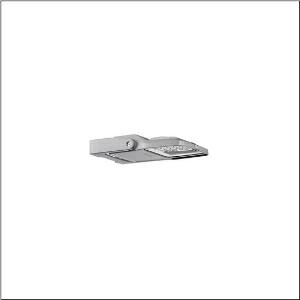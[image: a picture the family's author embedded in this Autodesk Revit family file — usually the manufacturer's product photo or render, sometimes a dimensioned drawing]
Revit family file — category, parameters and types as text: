
# Revit family: floodlight_fl_21_iq_micro___pl33t_5xa7761a2f2a_98c0
name_source: partatom
category: Lighting Fixtures
units: mm (PartAtom-declared; Revit-internal decimal feet)

## family parameters
Cut with Voids When Loaded = No
Host = Face
Light Source = No
Part Type = Normal
Room Calculation Point = No
Round Connector Dimension = Use Diameter
Shared = No

## types (1)
- --- (1 x LED, 2930 lm, 23.1 W, 3000K)
    Apparent Load = 23 VA
    CIE Flux Codes = 26 75 99 100 100
    Color Rendering = 70
    Color Temperature = 3000K
    Default Elevation = 1800 mm
    Description = Floodlight FL 21 iQ micro, floodlight, primary light control with lens, of PMMA, primary optical cover: protective disc, of toughened safety glass, transparent, light distribution: PL33T, light emission: direct distribution, installation type: surface-mounted, LED, High Power LED, rated luminous flux: 2.930lm, luminous efficacy: 127lm/W, light colour: 730, colour temperature: 3000K, control: optimised constant luminous flux control (CLO 2.0), Desk-Remote (wireless, voltage-free reading and setting of iQ features in the workshop via application-optimized NFC function/RFID function), Light-Fading, Smart-Wire, Night-Set, Lumen-Switch, Temp-Guard, Auto-Match, with terminal, 6-pole, mains connection: 220..240V, AC, 50/60Hz, start of lifetime: 23W, end of service life: 24W, reduction: 11W, luminaire housing, of diecast aluminium, powder-coated, Siteco® metallic grey (DB 702S), corrosivity category C5 mid according to DIN EN ISO 12944, sealing non-destructively replaceable, design bracket, of diecast aluminium, powder-coated, Siteco® metallic grey (DB 702S), protection rating (complete): IP66, insulation class (complete): insulation class II (safety insulation), certification: CE, ENEC, VDE, protection symbol: D, impact resistance: IK07, permissible operating ambient temperature: -40..+40°C, permissible operating ambient temperature for outdoor applications: -40..+50°C, standard: DIN EN 12944, LABS conformity tested according to VDMA 24364:2018-05, packaging unit: 1 piece

Light Distribution: PL33T
    Height = 65 mm
    Lamp = 1 x LED
    Lamp Light Flux = 2930 lm
    Lamp Power = 23.1 W
    Lamp count = 1
    Length = 312 mm
    Luminous efficacy = 127 lm/W
    Manufacturer = Siteco
    ModVariant = No
    Model = 5XA7761A2F2A
    Mounting Place = Wall
    Mounting Type = Surface mounted
    Number of Poles = 1
    OnlyDefault = Yes
    Power Factor = 1
    Product Name = Floodlight FL 21 iQ micro | PL33T
    Product group = floodlight | wall mounted
    ProductGroupID = 2001
    Protection Class = Protection class II
    Protection Degree = IP 66
    RLX_Detail_Level = 1
    RLX_Emergency_Light_Flux = 0 lm
    RLX_Emergency_Type = 0
    RLX_Emergency_Type_DB = No
    RlxData = <blob elided: 97241 chars, md5=ee019f52>
    Socket = socket
    Standby Power = 0 W
    System Light Flux = 2930 lm
    System Power = 23 W
    Type Comments = factory setting: luminous flux: 100 % | dim-lin: 254 | 455 mA
    Type Image = l_1006878.jpg
    URL = http://relux.com
    VarID = @adj_098419
    Voltage = 0 V
    Weight = 0.00 kg
    Width = 230 mm

## geometry (parser evidence)
native form markers: Blend x4, Sweep x11
no freeform markers — native parametric forms only
